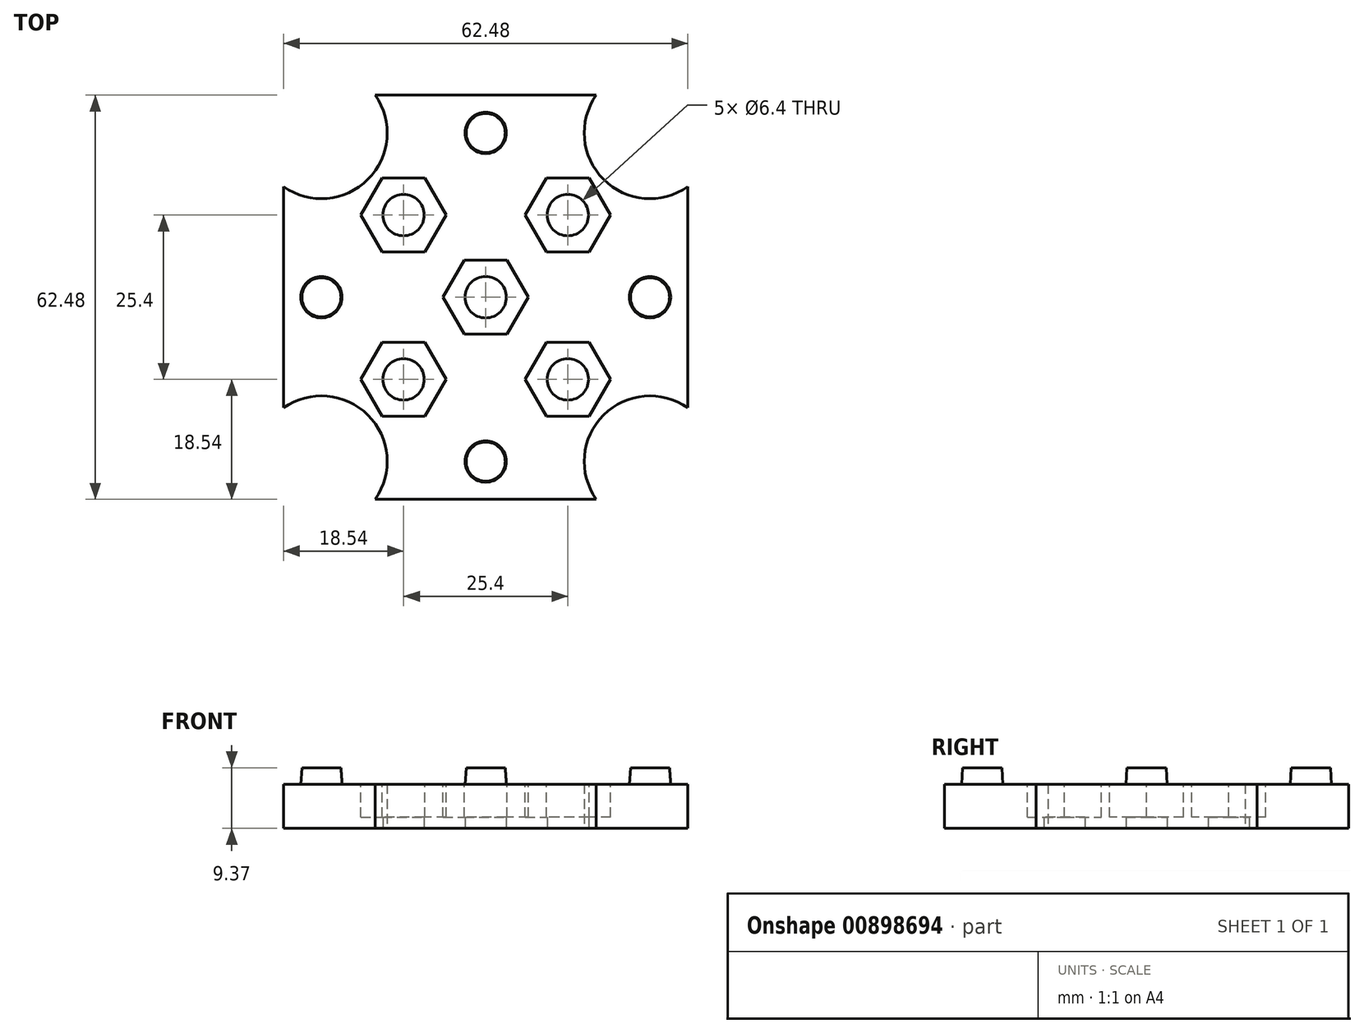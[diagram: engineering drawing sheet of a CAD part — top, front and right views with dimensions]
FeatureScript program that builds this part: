
annotation { "Feature Type Name" : "Feature", "Feature Type Description" : "" }
export const myFeature = defineFeature(function(context is Context, id is Id, definition is map)
    precondition{}
    {
        {
            var Q0;
            Q0=qCreatedBy(makeId("Top.planeOp"),FACE);
            var sketch = newSketch(context, id + "F0", { "sketchPlane" : qUnion([Q0])});
            skLineSegment(sketch, "E0.bottom", {"start": v(-25.4, 25.4) * mm, "end": v(25.4, 25.4) * mm, "construction": true});
            skLineSegment(sketch, "E0.top", {"start": v(-25.4, -25.4) * mm, "end": v(25.4, -25.4) * mm, "construction": true});
            skLineSegment(sketch, "E0.left", {"start": v(-25.4, 25.4) * mm, "end": v(-25.4, -25.4) * mm, "construction": true});
            skLineSegment(sketch, "E0.right", {"start": v(25.4, 25.4) * mm, "end": v(25.4, -25.4) * mm, "construction": true});
            skLineSegment(sketch, "E1", {"start": v(0, 25.4) * mm, "end": v(0, -25.4) * mm, "construction": true});
            skLineSegment(sketch, "E2", {"start": v(-25.4, 0) * mm, "end": v(25.4, 0) * mm, "construction": true});
            skCircle(sketch, "E3", {"center": v(-25.4, -25.4) * mm, "radius": 10.16 * mm});
            skArc(sketch, "E4", {"start": v(-31.24, 17.09) * mm, "mid": v(-18.22, 18.22) * mm, "end": v(-17.09, 31.24) * mm});
            skCircle(sketch, "E5", {"center": v(25.4, -25.4) * mm, "radius": 10.16 * mm});
            skCircle(sketch, "E6", {"center": v(25.4, 25.4) * mm, "radius": 10.16 * mm});
            skCircle(sketch, "E7", {"center": v(0, 0) * mm, "radius": 3.2 * mm});
            skCircle(sketch, "E8", {"center": v(-12.7, -12.7) * mm, "radius": 3.2 * mm});
            skCircle(sketch, "E9.0.1.0", {"center": v(-12.7, 12.7) * mm, "radius": 3.2 * mm});
            skCircle(sketch, "E9.1.0.0", {"center": v(12.7, -12.7) * mm, "radius": 3.2 * mm});
            skCircle(sketch, "E9.1.1.0", {"center": v(12.7, 12.7) * mm, "radius": 3.2 * mm});
            skLineSegment(sketch, "E9.direction1", {"start": v(-12.7, -12.7) * mm, "end": v(12.7, -12.7) * mm, "construction": true});
            skLineSegment(sketch, "E9.direction2", {"start": v(-12.7, -12.7) * mm, "end": v(-12.7, 12.7) * mm, "construction": true});
            skCircle(sketch, "E10", {"center": v(0, 0) * mm, "radius": 6.86 * mm});
            skCircle(sketch, "E11", {"center": v(-25.4, 0) * mm, "radius": 3.2 * mm});
            skCircle(sketch, "E12", {"center": v(0, 25.4) * mm, "radius": 3.2 * mm});
            skCircle(sketch, "E13", {"center": v(25.4, 0) * mm, "radius": 3.2 * mm});
            skCircle(sketch, "E14", {"center": v(0, -25.4) * mm, "radius": 3.2 * mm});
            skLineSegment(sketch, "E15.bottom", {"start": v(-31.24, 31.24) * mm, "end": v(31.24, 31.24) * mm});
            skLineSegment(sketch, "E15.top", {"start": v(-31.24, -31.24) * mm, "end": v(31.24, -31.24) * mm});
            skLineSegment(sketch, "E15.left", {"start": v(-31.24, 31.24) * mm, "end": v(-31.24, -31.24) * mm});
            skLineSegment(sketch, "E15.right", {"start": v(31.24, 31.24) * mm, "end": v(31.24, -31.24) * mm});
            skLineSegment(sketch, "E16", {"start": v(0, 25.4) * mm, "end": v(0, 31.24) * mm, "construction": true});
            skLineSegment(sketch, "E17", {"start": v(25.4, 0) * mm, "end": v(31.24, 0) * mm, "construction": true});
            skSolve(sketch);
        }
        {
            var Q0;
            {var subQ5=sQuery(id+"F0.wireOp",EDGE,"E4");Q0=makeQuery(id+"F0.imprint","IMPRINT",FACE,{"disambiguationData":[TD([[makeQuery(id+"F0.imprint","IMPRINT",EDGE,{"derivedFrom":subQ5}),-1.0]])]});}
            var Q1;
            Q1=makeQuery(id+"F0.imprint","IMPRINT",FACE,{"disambiguationData":[TD([[makeQuery(id+"F0.imprint","IMPRINT",EDGE,{"derivedFrom":sQuery(id+"F0.wireOp",EDGE,"E7")}),-1.0]])]});
            extrude(context, id + "F1", {"entities" : qUnion([Q0, Q1]), "depth" : 6.83 * mm, "offsetDistance" : 25.4 * mm});
        }
        {
            var Q0;
            Q0=makeQuery(id+"F0.imprint","IMPRINT",FACE,{"disambiguationData":[TD([[makeQuery(id+"F0.imprint","IMPRINT",EDGE,{"derivedFrom":sQuery(id+"F0.wireOp",EDGE,"E11")}),1.0]])]});
            var Q1;
            Q1=makeQuery(id+"F0.imprint","IMPRINT",FACE,{"disambiguationData":[TD([[makeQuery(id+"F0.imprint","IMPRINT",EDGE,{"derivedFrom":sQuery(id+"F0.wireOp",EDGE,"E14")}),1.0]])]});
            var Q2;
            Q2=makeQuery(id+"F0.imprint","IMPRINT",FACE,{"disambiguationData":[TD([[makeQuery(id+"F0.imprint","IMPRINT",EDGE,{"derivedFrom":sQuery(id+"F0.wireOp",EDGE,"E13")}),1.0]])]});
            var Q3;
            Q3=makeQuery(id+"F0.imprint","IMPRINT",FACE,{"disambiguationData":[TD([[makeQuery(id+"F0.imprint","IMPRINT",EDGE,{"derivedFrom":sQuery(id+"F0.wireOp",EDGE,"E12")}),1.0]])]});
            extrude(context, id + "F2", {"entities" : qUnion([Q0, Q1, Q2, Q3]), "operationType" : NewBodyOperationType.ADD, "depth" : 9.37 * mm, "offsetDistance" : 25.4 * mm});
        }
        {
            var Q0;
            Q0=makeQuery(id+"F1.opExtrude","CAP_FACE",FACE,{"disambiguationData":[OSD([sQuery(id+"F0.wireOp",EDGE,"E3"),sQuery(id+"F0.wireOp",EDGE,"E4"),sQuery(id+"F0.wireOp",EDGE,"E5"),sQuery(id+"F0.wireOp",EDGE,"E6"),sQuery(id+"F0.wireOp",EDGE,"E7"),sQuery(id+"F0.wireOp",EDGE,"E8"),sQuery(id+"F0.wireOp",EDGE,"E9.0.1.0"),sQuery(id+"F0.wireOp",EDGE,"E9.1.0.0"),sQuery(id+"F0.wireOp",EDGE,"E9.1.1.0"),sQuery(id+"F0.wireOp",EDGE,"E11"),sQuery(id+"F0.wireOp",EDGE,"E12"),sQuery(id+"F0.wireOp",EDGE,"E13"),sQuery(id+"F0.wireOp",EDGE,"E14"),sQuery(id+"F0.wireOp",EDGE,"E15.bottom"),sQuery(id+"F0.wireOp",EDGE,"E15.top"),sQuery(id+"F0.wireOp",EDGE,"E15.left"),sQuery(id+"F0.wireOp",EDGE,"E15.right")])],"isStart":false});
            var sketch = newSketch(context, id + "F3", { "sketchPlane" : qUnion([Q0])});
            skCircle(sketch, "E18.0", {"center": v(0, 0) * mm, "radius": 6.86 * mm, "construction": true});
            skCircle(sketch, "E19.0", {"center": v(12.7, 12.7) * mm, "radius": 3.2 * mm, "construction": true});
            skCircle(sketch, "E20.0", {"center": v(-12.7, 12.7) * mm, "radius": 3.2 * mm, "construction": true});
            skCircle(sketch, "E21.0", {"center": v(-12.7, -12.7) * mm, "radius": 3.2 * mm, "construction": true});
            skCircle(sketch, "E22.0", {"center": v(12.7, -12.7) * mm, "radius": 3.2 * mm, "construction": true});
            skCircle(sketch, "E23.cCircle", {"center": v(-12.7, 12.7) * mm, "radius": 6.6 * mm, "construction": true});
            skLineSegment(sketch, "E23.0", {"start": v(-6.1, 12.7) * mm, "end": v(-9.4, 6.98) * mm});
            skLineSegment(sketch, "E23.1", {"start": v(-9.4, 6.98) * mm, "end": v(-16, 6.98) * mm});
            skLineSegment(sketch, "E23.2", {"start": v(-16, 6.98) * mm, "end": v(-19.3, 12.7) * mm});
            skLineSegment(sketch, "E23.3", {"start": v(-19.3, 12.7) * mm, "end": v(-16, 18.42) * mm});
            skLineSegment(sketch, "E23.4", {"start": v(-16, 18.42) * mm, "end": v(-9.4, 18.42) * mm});
            skLineSegment(sketch, "E23.5", {"start": v(-9.4, 18.42) * mm, "end": v(-6.1, 12.7) * mm});
            skCircle(sketch, "E24.cCircle", {"center": v(12.7, 12.7) * mm, "radius": 6.6 * mm, "construction": true});
            skLineSegment(sketch, "E24.0", {"start": v(6.1, 12.7) * mm, "end": v(9.4, 18.42) * mm});
            skLineSegment(sketch, "E24.1", {"start": v(9.4, 18.42) * mm, "end": v(16, 18.42) * mm});
            skLineSegment(sketch, "E24.2", {"start": v(16, 18.42) * mm, "end": v(19.3, 12.7) * mm});
            skLineSegment(sketch, "E24.3", {"start": v(19.3, 12.7) * mm, "end": v(16, 6.98) * mm});
            skLineSegment(sketch, "E24.4", {"start": v(16, 6.98) * mm, "end": v(9.4, 6.98) * mm});
            skLineSegment(sketch, "E24.5", {"start": v(9.4, 6.98) * mm, "end": v(6.1, 12.7) * mm});
            skCircle(sketch, "E25.cCircle", {"center": v(-12.7, -12.7) * mm, "radius": 6.6 * mm, "construction": true});
            skLineSegment(sketch, "E25.0", {"start": v(-6.1, -12.7) * mm, "end": v(-9.4, -18.42) * mm});
            skLineSegment(sketch, "E25.1", {"start": v(-9.4, -18.42) * mm, "end": v(-16, -18.42) * mm});
            skLineSegment(sketch, "E25.2", {"start": v(-16, -18.42) * mm, "end": v(-19.3, -12.7) * mm});
            skLineSegment(sketch, "E25.3", {"start": v(-19.3, -12.7) * mm, "end": v(-16, -6.98) * mm});
            skLineSegment(sketch, "E25.4", {"start": v(-16, -6.98) * mm, "end": v(-9.4, -6.98) * mm});
            skLineSegment(sketch, "E25.5", {"start": v(-9.4, -6.98) * mm, "end": v(-6.1, -12.7) * mm});
            skCircle(sketch, "E26.cCircle", {"center": v(12.7, -12.7) * mm, "radius": 6.6 * mm, "construction": true});
            skLineSegment(sketch, "E26.0", {"start": v(6.1, -12.7) * mm, "end": v(9.4, -6.98) * mm});
            skLineSegment(sketch, "E26.1", {"start": v(9.4, -6.98) * mm, "end": v(16, -6.98) * mm});
            skLineSegment(sketch, "E26.2", {"start": v(16, -6.98) * mm, "end": v(19.3, -12.7) * mm});
            skLineSegment(sketch, "E26.3", {"start": v(19.3, -12.7) * mm, "end": v(16, -18.42) * mm});
            skLineSegment(sketch, "E26.4", {"start": v(16, -18.42) * mm, "end": v(9.4, -18.42) * mm});
            skLineSegment(sketch, "E26.5", {"start": v(9.4, -18.42) * mm, "end": v(6.1, -12.7) * mm});
            skCircle(sketch, "E27.cCircle", {"center": v(0, 0) * mm, "radius": 6.6 * mm, "construction": true});
            skLineSegment(sketch, "E27.0", {"start": v(6.6, 0) * mm, "end": v(3.3, -5.72) * mm});
            skLineSegment(sketch, "E27.1", {"start": v(3.3, -5.72) * mm, "end": v(-3.3, -5.72) * mm});
            skLineSegment(sketch, "E27.2", {"start": v(-3.3, -5.72) * mm, "end": v(-6.6, 0) * mm});
            skLineSegment(sketch, "E27.3", {"start": v(-6.6, 0) * mm, "end": v(-3.3, 5.72) * mm});
            skLineSegment(sketch, "E27.4", {"start": v(-3.3, 5.72) * mm, "end": v(3.3, 5.72) * mm});
            skLineSegment(sketch, "E27.5", {"start": v(3.3, 5.72) * mm, "end": v(6.6, 0) * mm});
            skSolve(sketch);
        }
        {
            var Q0;
            Q0=makeQuery(id+"F3.imprint","IMPRINT",FACE,{"disambiguationData":[TD([[makeQuery(id+"F3.imprint","IMPRINT",EDGE,{"derivedFrom":sQuery(id+"F3.wireOp",EDGE,"E23.0")}),-1.0]])]});
            var Q1;
            Q1=makeQuery(id+"F3.imprint","IMPRINT",FACE,{"disambiguationData":[TD([[makeQuery(id+"F3.imprint","IMPRINT",EDGE,{"derivedFrom":sQuery(id+"F3.wireOp",EDGE,"E24.0")}),-1.0]])]});
            var Q2;
            Q2=makeQuery(id+"F3.imprint","IMPRINT",FACE,{"disambiguationData":[TD([[makeQuery(id+"F3.imprint","IMPRINT",EDGE,{"derivedFrom":sQuery(id+"F3.wireOp",EDGE,"E25.0")}),-1.0]])]});
            var Q3;
            Q3=makeQuery(id+"F3.imprint","IMPRINT",FACE,{"disambiguationData":[TD([[makeQuery(id+"F3.imprint","IMPRINT",EDGE,{"derivedFrom":sQuery(id+"F3.wireOp",EDGE,"E26.0")}),-1.0]])]});
            var Q4;
            Q4=makeQuery(id+"F3.imprint","IMPRINT",FACE,{"disambiguationData":[TD([[makeQuery(id+"F3.imprint","IMPRINT",EDGE,{"derivedFrom":sQuery(id+"F3.wireOp",EDGE,"E18.0")}),1.0]])]});
            var Q5;
            Q5=makeQuery(id+"F3.imprint","IMPRINT",FACE,{"disambiguationData":[TD([[makeQuery(id+"F3.imprint","IMPRINT",EDGE,{"derivedFrom":sQuery(id+"F3.wireOp",EDGE,"E27.0")}),-1.0]])]});
            extrude(context, id + "F4", {"entities" : qUnion([Q0, Q1, Q2, Q3, Q4, Q5]), "operationType" : NewBodyOperationType.REMOVE, "oppositeDirection" : true, "depth" : 5.08 * mm, "offsetDistance" : 25.4 * mm});
        }
        {
            var Q0;
            Q0=makeQuery(id+"F2.opExtrude","CAP_EDGE",EDGE,{"disambiguationData":[OSD([sQuery(id+"F0.wireOp",EDGE,"E11")])],"isStart":false});
            var Q1;
            Q1=makeQuery(id+"F2.opExtrude","CAP_EDGE",EDGE,{"disambiguationData":[OSD([sQuery(id+"F0.wireOp",EDGE,"E12")])],"isStart":false});
            var Q2;
            Q2=makeQuery(id+"F2.opExtrude","CAP_EDGE",EDGE,{"disambiguationData":[OSD([sQuery(id+"F0.wireOp",EDGE,"E13")])],"isStart":false});
            var Q3;
            Q3=makeQuery(id+"F2.opExtrude","CAP_EDGE",EDGE,{"disambiguationData":[OSD([sQuery(id+"F0.wireOp",EDGE,"E14")])],"isStart":false});
            chamfer(context, id + "F5", {"entities" : qUnion([Q0, Q1, Q2, Q3]), "chamferType" : ChamferType.TWO_OFFSETS, "width1" : 0.18 * mm, "oppositeDirection" : false, "width2" : 2.54 * mm, "tangentPropagation" : true});
        }
    });
